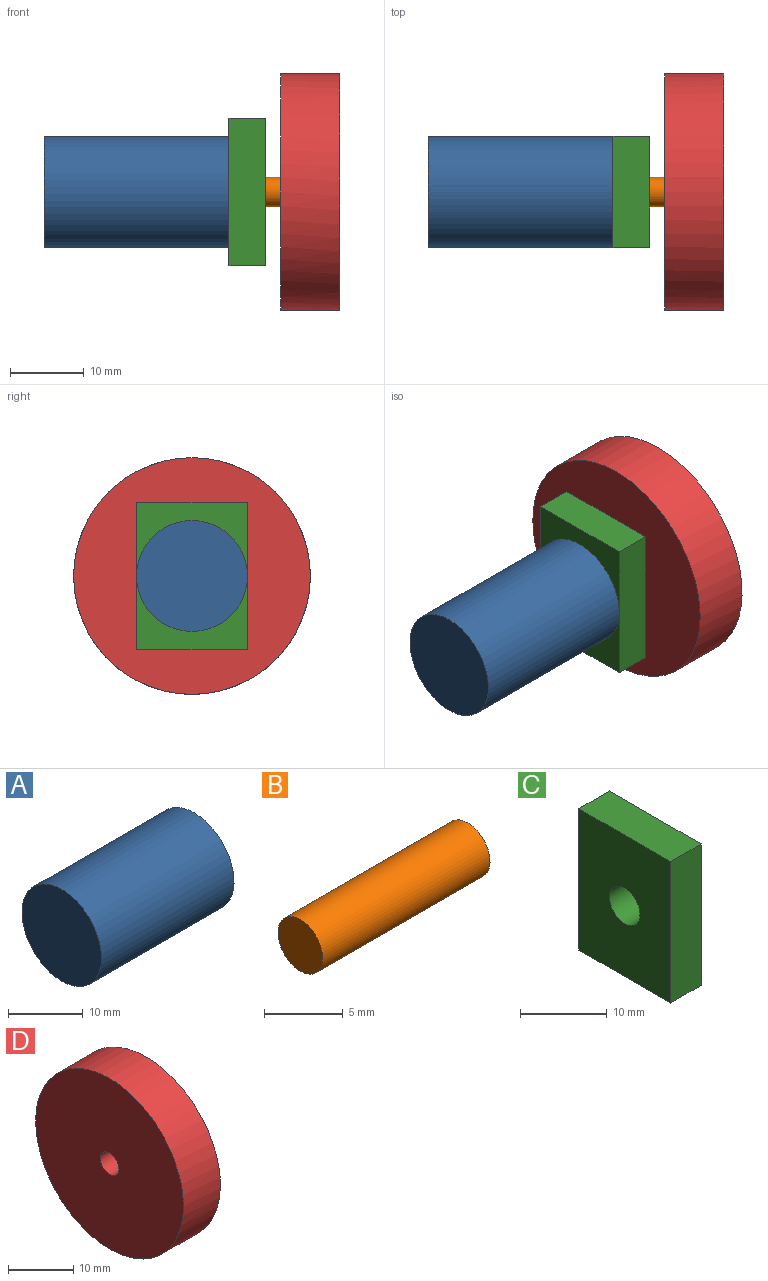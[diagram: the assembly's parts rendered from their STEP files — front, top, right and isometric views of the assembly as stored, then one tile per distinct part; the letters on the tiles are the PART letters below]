
ASSEMBLY  parts=4 mates=3
PART A: 3 faces, bbox 25x15x15 mm
  f0: cylinder r=7.5mm len=25mm, axis (1,0,0), area 1178.1mm2, adj f1,f2
  f1: plane 15x15mm, normal (-1,0,0), area 176.7mm2, adj f0
  f2: plane 15x15mm, normal (1,0,0), area 176.7mm2, adj f0
PART B: 3 faces, bbox 15x4x4 mm
  f0: cylinder r=2mm len=15mm, axis (-1,0,0), area 188.5mm2, adj f1,f2
  f1: plane 4x4mm, normal (1,0,0), area 12.6mm2, adj f0
  f2: plane 4x4mm, normal (-1,0,0), area 12.6mm2, adj f0
PART C: 7 faces, bbox 5x15x20 mm
  f0: plane 15x5mm, normal (0,0,-1), area 75mm2, adj f1,f3,f5,f6
  f1: plane 20x5mm, normal (0,1,0), area 100mm2, adj f0,f2,f5,f6
  f2: plane 15x5mm, normal (0,0,1), area 75mm2, adj f1,f3,f5,f6
  f3: plane 20x5mm, normal (0,-1,0), area 100mm2, adj f0,f2,f5,f6
  f4: cylinder r=2.5mm len=5mm, axis (1,0,0), area 78.5mm2, adj f5,f6
  f5: plane 20x15mm, normal (-1,0,0), area 280.4mm2, adj f0,f1,f2,f3,f4
  f6: plane 20x15mm, normal (1,0,0), area 280.4mm2, adj f0,f1,f2,f3,f4
PART D: 4 faces, bbox 8x32x32 mm
  f0: plane 32x32mm, normal (-1,0,0), area 791.7mm2, adj f2,f3
  f1: plane 32x32mm, normal (1,0,0), area 791.7mm2, adj f2,f3
  f2: cylinder r=2mm len=8mm, axis (-1,0,0), area 100.5mm2, adj f0,f1
  f3: cylinder r=16mm len=32mm, axis (-1,0,0), area 804.2mm2, adj f0,f1
PLACE A at identity fixed
PLACE B at identity
PLACE C at identity
PLACE D at identity
MATE fastened D.f2 <-> B.f0  axis (1,0,0) through (10,7.5,13)mm
MATE fastened A.f0 <-> B.f0  axis (1,0,0) through (-5,7.5,13)mm
MATE fastened C.f4 <-> A.f0  axis (-1,0,0) through (-5,7.5,13)mm
